# Revit family: Spine_Desks-Teknion-RMDDL_Spine_Desk_Shared_In_Line_Position-R2019
name_source: partatom
category: Furniture
units: mm (PartAtom-declared; Revit-internal decimal feet)

## family parameters
Always vertical = Yes
Cut with Voids When Loaded = No
OmniClass Number = 23.40.20.00
OmniClass Title = General Furniture and Specialties
Room Calculation Point = No
Shared = Yes
Work Plane-Based = No

## types (7) — shared parameters
Assembly Code = E2020200
Manufacturer = Teknion
Manufacturer Fax = 416.661.4586
Part Number = RMDDL
Product Documentation Link = https://www.teknion.com
Product Line = Expansion Desking
Product Page URL = https://www.teknion.com
Series = Expansion Desking
Sustainability Data = https://www.teknion.com
URL = www.teknion.com
Unit Weight URL = http://www.teknion.com
Warranty = http://www.teknion.com

## per-type parameters (varying)
| type | Access Door | Both Ends Rectangular Grommet | Centered Rectangular Grommet | Description | Left Access Door | Middle Access Door | Model | Offset Left Access Door | Offset Right Access Door | Right Access Door |
| Rectangular Grommets Both Ends, Raised Modesty Panel | No | Yes | No | Spine Desk - Shared - In Line Position, Raised Modesty Panel, Rectangular Grommets Both Ends | No | No | RMDDL_RB_____ | No | No | No |
| Rectangular Grommets Centered, Raised Modesty Panel | No | No | Yes | Spine Desk - Shared - In Line Position, Raised Modesty Panel, Rectangular Grommets Centered | No | No | RMDDL_RC_____ | No | No | No |
| Access Door Offset Left, Raised Modesty Panel | Yes | No | No | Spine Desk - Shared - In Line Position, Raised Modesty Panel, Access Door Offset Left | No | No | RMDDL_RD_____ | Yes | No | No |
| Access Door Offset Right, Raised Modesty Panel | Yes | No | No | Spine Desk - Shared - In Line Position, Raised Modesty Panel, Access Door Offset Right | No | No | RMDDL_RE_____ | No | Yes | No |
| Access Door Left, Raised Modesty Panel | Yes | No | No | Spine Desk - Shared - In Line Position, Raised Modesty Panel, Access Door Left | Yes | No | RMDDL_RL_____ | No | No | No |
| Access Door Middle, Raised Modesty Panel | Yes | No | No | Spine Desk - Shared - In Line Position, Raised Modesty Panel, Access Door Middle | No | Yes | RMDDL_RM_____ | No | No | No |
| Access Door Right, Raised Modesty Panel | Yes | No | No | Spine Desk - Shared - In Line Position, Raised Modesty Panel, Access Door Right | No | No | RMDDL_RR_____ | No | No | Yes |

## geometry (parser evidence)
native form markers: Sweep x4
no freeform markers — native parametric forms only
